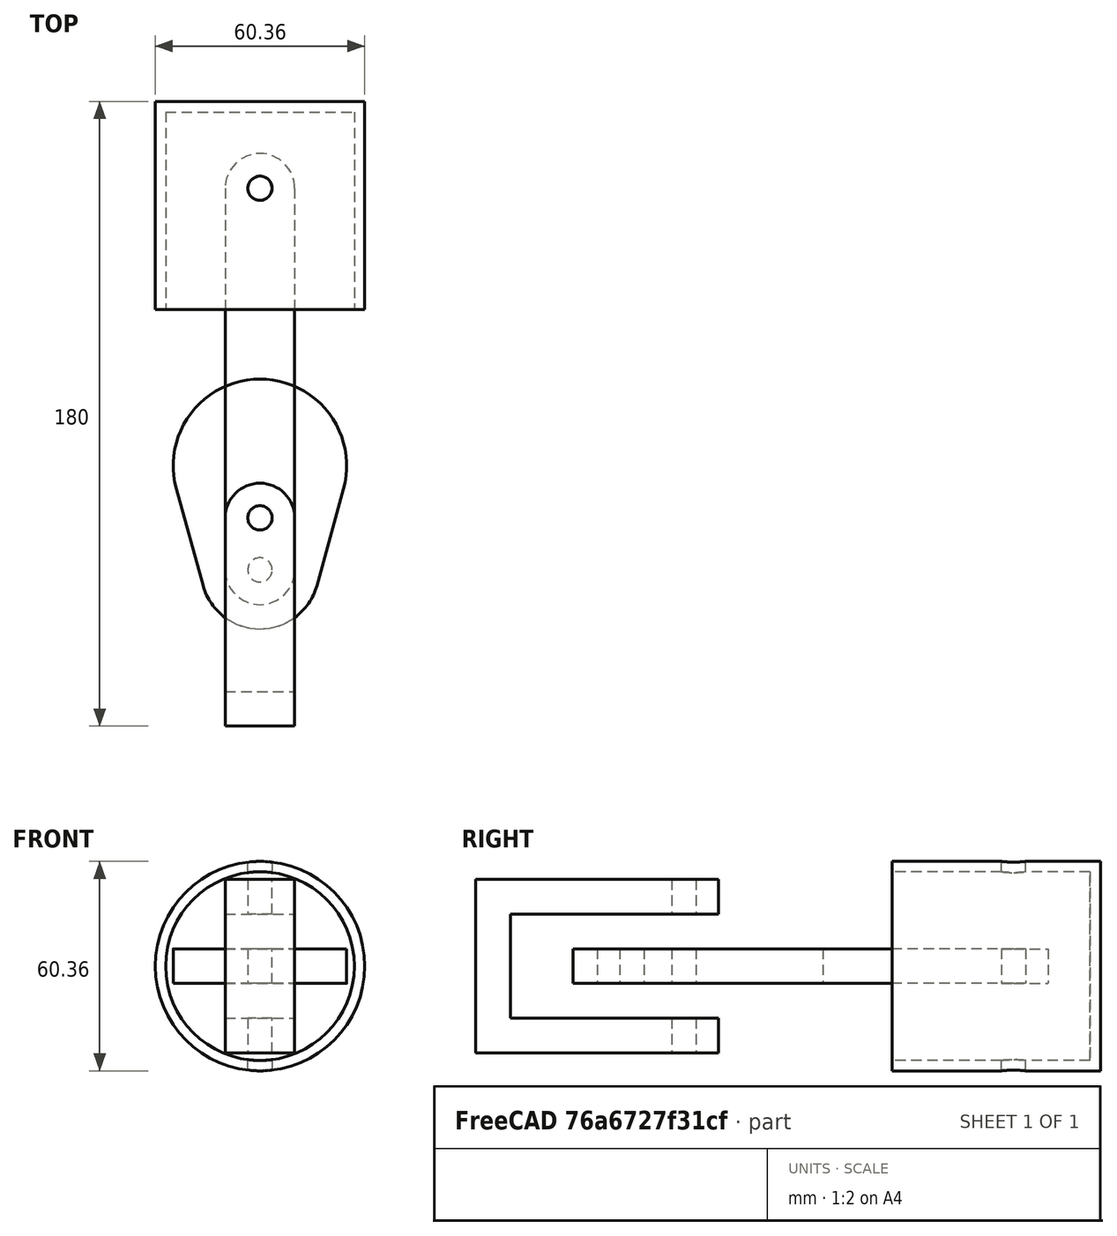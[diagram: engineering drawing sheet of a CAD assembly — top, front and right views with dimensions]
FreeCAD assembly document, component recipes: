
FREECAD ASSEMBLY — COMPONENT RECIPES ("piston_head_assembly")

This assembly document has 5 components, labeled P0..P4 below (a component is one placed body or linked part). 5 of them carry a construction recipe — the FreeCAD feature program that regenerates the part from scratch, quoted from this document or its linked companion documents; the rest are supplied as boundary geometry only. No exploded tour is included for this assembly.
COMPONENT P0 — recipe-attached ("Crank001", modeled in this document).
Construction recipe (the document's own serialized feature program — sketch geometry with constraints, then the solid features built on it; lengths are millimeters unless a unit is written):

FEATURE [PartDesign::SubShapeBinder] Binder002
  BindCopyOnChange = 0
  BindMode = 0
  ClaimChildren = false
  Context = -> Body002 [Binder002.]
  Fuse = false
  MakeFace = false
  OffsetFill = false
  OffsetIntersection = false
  OffsetJoinType = 0
  OffsetOpenResult = false
  PartialLoad = false
  Refine = true
  Relative = true
  Support = -> [Sketch]
  _Version = 2
FEATURE [Sketcher::SketchObject] Sketch004
  ArcFitTolerance = 1e-06
  AttachmentSupport = -> [XY_Plane002]
  ExternalGeometry = -> [Binder002]
  FullyConstrained = true
  MakeInternals = false
  MapMode = 5
  sketch-geometry (6):
    g0: Circle CenterX=0 CenterY=-40 CenterZ=0 NormalX=0 NormalY=0 NormalZ=1 AngleXU=0 Radius=3.5
    g1: Circle CenterX=0 CenterY=-55 CenterZ=0 NormalX=0 NormalY=0 NormalZ=1 AngleXU=0 Radius=3.5
    g2: LineSegment StartX=-24.0947 StartY=-31.6667 StartZ=0 EndX=-16.3844 EndY=-59.5333 EndZ=0
    g3: ArcOfCircle CenterX=2e-16 CenterY=-55 CenterZ=0 NormalX=0 NormalY=0 NormalZ=1 AngleXU=0 Radius=17 StartAngle=3.41153 EndAngle=6.01325
    g4: LineSegment StartX=16.3844 StartY=-59.5333 StartZ=0 EndX=24.0947 EndY=-31.6667 EndZ=0
    g5: ArcOfCircle CenterX=1.2308e-12 CenterY=-25 CenterZ=0 NormalX=0 NormalY=0 NormalZ=1 AngleXU=0 Radius=25 StartAngle=6.01325 EndAngle=9.69471
  constraints (12):
    c: Coincident(g0,g-7)
    c: Equal(g0,g-7)
    c: Coincident(g1,g-8)
    c: Equal(g1,g-8)
    c: Coincident(g-5,g2)
    c: Coincident(g2,g-6)
    c: Tangent(g2,g3) = -1.5708
    c: Coincident(g3,g-6)
    c: Tangent(g3,g4) = -1.5708
    c: Tangent(g4,g5) = -1.5708
    c: Coincident(g5,g2)
    c: PointOnObject(g-1,g5)
FEATURE [PartDesign::Pad] Pad001
  Direction = (0,0,1)
  Length = 10
  Length2 = 10
  Midplane = true
  Profile = -> Sketch004
  ReferenceAxis = -> Sketch004 [N_Axis]
  Refine = true
  Suppressed = false
  Type = 0
FEATURE [PartDesign::Body] Body002  label="Crank"
  AllowCompound = false
  Group = -> [Binder002,Sketch004,Pad001]
  Origin = -> Origin002
  Tip = -> Pad001
COMPONENT P1 — same part as P0; its construction recipe is shown at P0.
COMPONENT P2 — recipe-attached ("Link001", modeled in this document).
Construction recipe (the document's own serialized feature program — sketch geometry with constraints, then the solid features built on it; lengths are millimeters unless a unit is written):

FEATURE [PartDesign::SubShapeBinder] Binder
  BindCopyOnChange = 0
  BindMode = 0
  ClaimChildren = false
  Context = -> Body [Binder.]
  Fuse = false
  MakeFace = false
  OffsetFill = false
  OffsetIntersection = false
  OffsetJoinType = 0
  OffsetOpenResult = false
  PartialLoad = false
  Refine = true
  Relative = true
  Support = -> [Sketch]
  _Version = 2
FEATURE [Sketcher::SketchObject] Sketch001
  ArcFitTolerance = 1e-06
  AttachmentSupport = -> [XY_Plane]
  ExternalGeometry = -> [Binder]
  FullyConstrained = true
  MakeInternals = false
  MapMode = 5
  sketch-geometry (6):
    g0: LineSegment StartX=-10 StartY=55 StartZ=0 EndX=-10 EndY=-55 EndZ=0
    g1: LineSegment StartX=10 StartY=55 StartZ=0 EndX=10 EndY=-55 EndZ=0
    g2: ArcOfCircle CenterX=-1e-16 CenterY=55 CenterZ=0 NormalX=0 NormalY=0 NormalZ=1 AngleXU=0 Radius=10 StartAngle=2e-16 EndAngle=3.14159
    g3: ArcOfCircle CenterX=1e-16 CenterY=-55 CenterZ=0 NormalX=0 NormalY=0 NormalZ=1 AngleXU=0 Radius=10 StartAngle=3.14159 EndAngle=6.28319
    g4: Circle CenterX=-1e-16 CenterY=55 CenterZ=0 NormalX=0 NormalY=0 NormalZ=1 AngleXU=0 Radius=3.5
    g5: Circle CenterX=1e-16 CenterY=-55 CenterZ=0 NormalX=0 NormalY=0 NormalZ=1 AngleXU=0 Radius=3.5
  constraints (14):
    c: Coincident(g2,g-6)
    c: Coincident(g2,g1)
    c: Coincident(g2,g0)
    c: Coincident(g3,g-8)
    c: Coincident(g3,g1)
    c: Coincident(g3,g0)
    c: Coincident(g4,g2)
    c: Coincident(g5,g3)
    c: Equal(g-4,g1)
    c: Coincident(g-4,g1)
    c: Coincident(g-7,g0)
    c: Equal(g-6,g4)
    c: Equal(g5,g-8)
    c: Equal(g-5,g0)
FEATURE [PartDesign::Pad] Pad
  Direction = (0,0,1)
  Length = 10
  Length2 = 10
  Midplane = true
  Profile = -> Sketch001
  ReferenceAxis = -> Sketch001 [N_Axis]
  Refine = true
  Suppressed = false
  Type = 0
FEATURE [PartDesign::Body] Body  label="Link"
  AllowCompound = false
  Group = -> [Binder,Sketch001,Pad]
  Origin = -> Origin
  Tip = -> Pad
COMPONENT P3 — recipe-attached ("Piston Head001", modeled in this document).
Construction recipe (the document's own serialized feature program — sketch geometry with constraints, then the solid features built on it; lengths are millimeters unless a unit is written):

FEATURE [PartDesign::SubShapeBinder] Binder001
  BindCopyOnChange = 0
  BindMode = 0
  ClaimChildren = false
  Context = -> Body001 [Binder001.]
  Fuse = false
  MakeFace = false
  OffsetFill = false
  OffsetIntersection = false
  OffsetJoinType = 0
  OffsetOpenResult = false
  PartialLoad = false
  Refine = true
  Relative = true
  Support = -> [Sketch]
  _Version = 2
FEATURE [Sketcher::SketchObject] Sketch002
  ArcFitTolerance = 1e-06
  AttachmentSupport = -> [XY_Plane001]
  ExternalGeometry = -> [Binder001]
  FullyConstrained = true
  MakeInternals = false
  MapMode = 5
  sketch-geometry (6):
    g0: LineSegment StartX=-30.18 StartY=20 StartZ=0 EndX=-30.18 EndY=80 EndZ=0
    g1: LineSegment StartX=-30.18 StartY=80 StartZ=0 EndX=0 EndY=80 EndZ=0
    g2: LineSegment StartX=0 StartY=80 StartZ=0 EndX=0 EndY=77 EndZ=0
    g3: LineSegment StartX=0 StartY=77 StartZ=0 EndX=-27.18 EndY=77 EndZ=0
    g4: LineSegment StartX=-27.18 StartY=77 StartZ=0 EndX=-27.18 EndY=20 EndZ=0
    g5: LineSegment StartX=-27.18 StartY=20 StartZ=0 EndX=-30.18 EndY=20 EndZ=0
  constraints (17):
    c: Coincident(g-5,g0)
    c: Coincident(g0,g-4)
    c: Coincident(g0,g1)
    c: Horizontal(g1)
    c: Coincident(g2,g3)
    c: Horizontal(g3)
    c: Coincident(g3,g4)
    c: PointOnObject(g4,g-5)
    c: Vertical(g4)
    c: Coincident(g4,g5)
    c: Coincident(g5,g0)
    c: Vertical(g2)
    c: PointOnObject(g1,g2)
    c: PointOnObject(g1,g-2)
    c: Distance(g0,g4) = 3
    c: Distance(g3,g1) = 3
    c: DistanceY(g2,g2) = 3
FEATURE [PartDesign::Revolution] Revolution
  Angle = 360
  Angle2 = 60
  Axis = (0,1,0)
  Base = (0,0,0)
  Profile = -> Sketch002
  ReferenceAxis = -> Sketch002 [V_Axis]
  Refine = true
  Suppressed = false
  Type = 0
FEATURE [Sketcher::SketchObject] Sketch003
  ArcFitTolerance = 1e-06
  AttachmentSupport = -> [XY_Plane001]
  ExternalGeometry = -> [Binder001]
  FullyConstrained = true
  MakeInternals = false
  MapMode = 5
  sketch-geometry (1):
    g0: Circle CenterX=0 CenterY=55 CenterZ=0 NormalX=0 NormalY=0 NormalZ=1 AngleXU=0 Radius=3.5
  constraints (2):
    c: Coincident(g0,g-3)
    c: Equal(g0,g-3)
FEATURE [PartDesign::Pocket] Pocket
  BaseFeature = -> Revolution
  Direction = (0,0,-1)
  Length = 5
  Length2 = 5
  Midplane = true
  Profile = -> Sketch003
  ReferenceAxis = -> Sketch003 [N_Axis]
  Refine = true
  Suppressed = false
  Type = 1
FEATURE [PartDesign::Body] Body001  label="Piston Head"
  AllowCompound = false
  Group = -> [Binder001,Sketch002,Revolution,Sketch003,Pocket]
  Origin = -> Origin001
  Tip = -> Pocket
COMPONENT P4 — recipe-attached ("mount001", modeled in this document).
Construction recipe (the document's own serialized feature program — sketch geometry with constraints, then the solid features built on it; lengths are millimeters unless a unit is written):

FEATURE [PartDesign::SubShapeBinder] Binder003
  BindCopyOnChange = 0
  BindMode = 0
  ClaimChildren = false
  Context = -> Body003 [Binder003.]
  Fuse = false
  MakeFace = false
  OffsetFill = false
  OffsetIntersection = false
  OffsetJoinType = 0
  OffsetOpenResult = false
  PartialLoad = false
  Refine = true
  Relative = true
  Support = -> [Sketch]
  _Version = 2
FEATURE [Sketcher::SketchObject] Sketch005
  ArcFitTolerance = 1e-06
  AttachmentSupport = -> [XY_Plane003]
  ExternalGeometry = -> [Binder003]
  FullyConstrained = true
  MakeInternals = false
  MapMode = 5
  sketch-geometry (5):
    g0: LineSegment StartX=-10 StartY=-40 StartZ=0 EndX=-10 EndY=-100 EndZ=0
    g1: LineSegment StartX=-10 StartY=-100 StartZ=0 EndX=10 EndY=-100 EndZ=0
    g2: LineSegment StartX=10 StartY=-100 StartZ=0 EndX=10 EndY=-40 EndZ=0
    g3: ArcOfCircle CenterX=-3.5369e-11 CenterY=-40 CenterZ=0 NormalX=0 NormalY=0 NormalZ=1 AngleXU=0 Radius=10 StartAngle=0 EndAngle=3.14159
    g4: Circle CenterX=-3.5369e-11 CenterY=-40 CenterZ=0 NormalX=0 NormalY=0 NormalZ=1 AngleXU=0 Radius=3.49997
  constraints (10):
    c: Tangent(g-6,g0) = -1.5708
    c: Coincident(g0,g1)
    c: Coincident(g1,g-4)
    c: Horizontal(g1)
    c: Coincident(g1,g2)
    c: Coincident(g2,g-6)
    c: Tangent(g2,g3) = -1.5708
    c: Coincident(g3,g0)
    c: Coincident(g4,g3)
    c: Tangent(g4,g-7)
FEATURE [PartDesign::Pad] Pad002
  Direction = (0,0,1)
  Length = 50
  Length2 = 10
  Midplane = true
  Profile = -> Sketch005
  ReferenceAxis = -> Sketch005 [N_Axis]
  Refine = true
  Suppressed = false
  Type = 0
FEATURE [Sketcher::SketchObject] Sketch006
  ArcFitTolerance = 1e-06
  AttachmentSupport = -> [Pad002]
  ExternalGeometry = -> [Pad002]
  FullyConstrained = true
  MakeInternals = false
  MapMode = 5
  Placement = pos=(-10,7.1e-15,0) rot=(0.57735,-0.57735,-0.57735;2.0944rad)
  sketch-geometry (4):
    g0: LineSegment StartX=25 StartY=15 StartZ=0 EndX=25 EndY=-15 EndZ=0
    g1: LineSegment StartX=25 StartY=-15 StartZ=0 EndX=90 EndY=-15 EndZ=0
    g2: LineSegment StartX=90 StartY=-15 StartZ=0 EndX=90 EndY=15 EndZ=0
    g3: LineSegment StartX=90 StartY=15 StartZ=0 EndX=25 EndY=15 EndZ=0
  constraints (12):
    c: Coincident(g0,g1)
    c: Coincident(g1,g2)
    c: Coincident(g2,g3)
    c: Coincident(g3,g0)
    c: Vertical(g0)
    c: Vertical(g2)
    c: Horizontal(g1)
    c: Horizontal(g3)
    c: Distance(g1,g3) = 30
    c: DistanceX(g2,g-3) = 10
    c: DistanceY(g2,g-3) = 10
    c: DistanceX(g0,g2) = 65
FEATURE [PartDesign::Pocket] Pocket001
  BaseFeature = -> Pad002
  Direction = (1,0,0)
  Length = 5
  Length2 = 5
  Midplane = true
  Profile = -> Sketch006
  ReferenceAxis = -> Sketch006 [N_Axis]
  Refine = true
  Suppressed = false
  Type = 1
FEATURE [PartDesign::Body] Body003  label="mount"
  AllowCompound = false
  Group = -> [Binder003,Sketch005,Pad002,Sketch006,Pocket001]
  Origin = -> Origin003
  Tip = -> Pocket001
PROVENANCE & LICENSES
A FreeCAD (.FCStd) document from a public repository crawl; recipes are the document's own serialized feature recipes (and, for linked parts, companion documents' recipes).
License: as declared in the source repository (recorded in the dataset sidecar).
